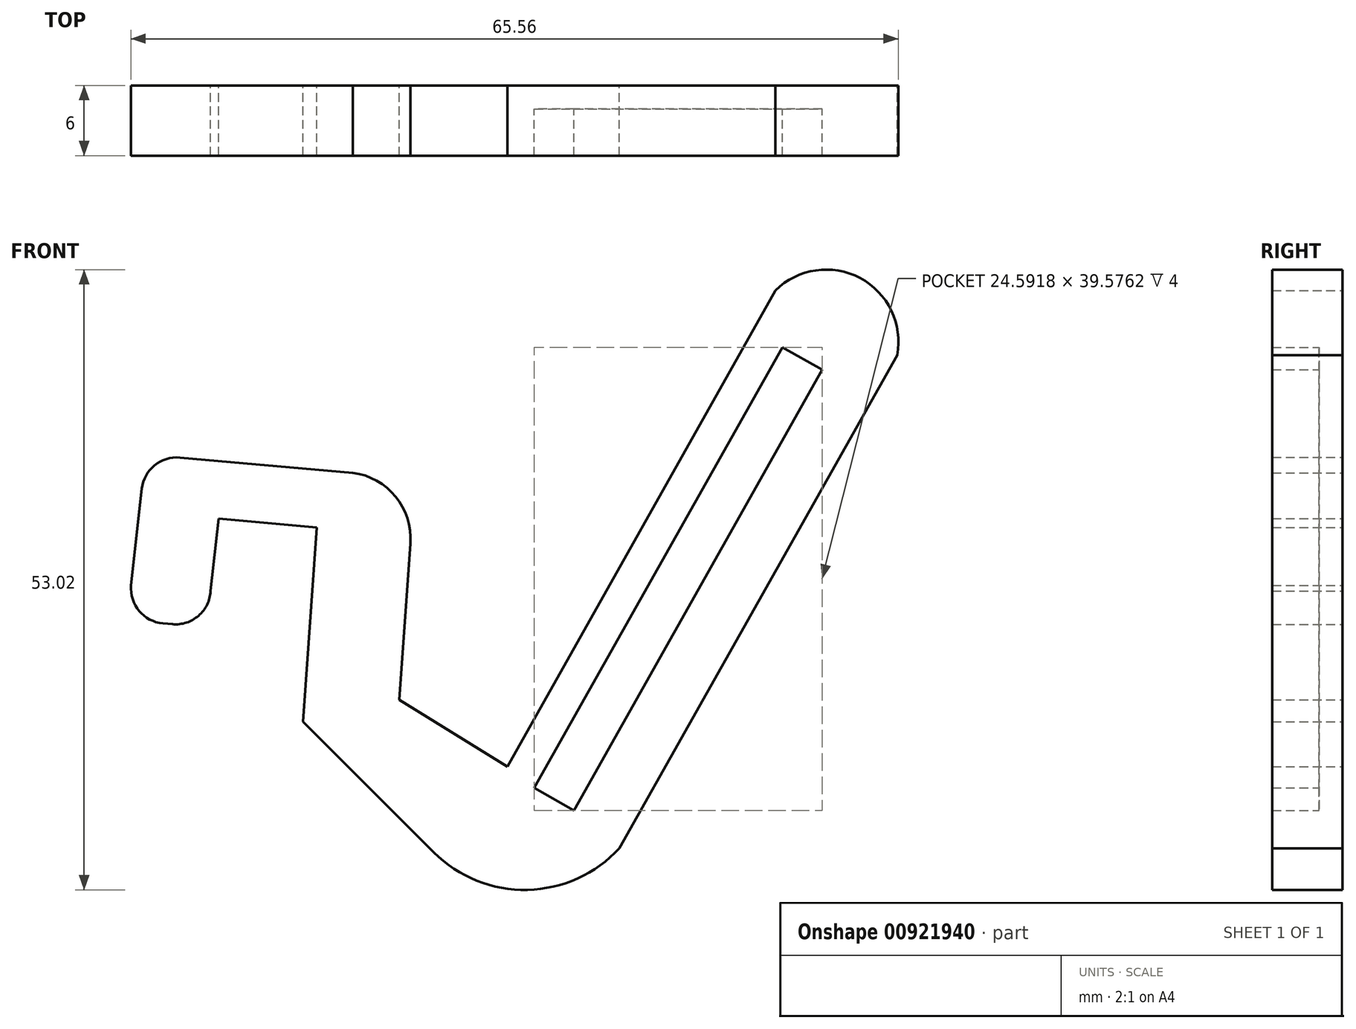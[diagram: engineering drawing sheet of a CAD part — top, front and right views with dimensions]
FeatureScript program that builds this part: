
annotation { "Feature Type Name" : "Feature", "Feature Type Description" : "" }
export const myFeature = defineFeature(function(context is Context, id is Id, definition is map)
    precondition{}
    {
        {
            var Q0;
            Q0=qCreatedBy(makeId("Front.planeOp"),FACE);
            var sketch = newSketch(context, id + "F0", { "sketchPlane" : qUnion([Q0])});
            skLineSegment(sketch, "E0", {"start": v(-33.3, 26.15) * mm, "end": v(-32.48, 26.08) * mm});
            skLineSegment(sketch, "E1", {"start": v(1.83, 10.17) * mm, "end": v(-1.57, 12.08) * mm});
            skLineSegment(sketch, "E2", {"start": v(-1.57, 12.08) * mm, "end": v(19.62, 49.74) * mm});
            skPoint(sketch, "E3.visualSharp", {"position": v(22.73, 46.46) * mm});
            skLineSegment(sketch, "E3.filletArc", {"start": v(24.58, 49.74) * mm, "end": v(24.58, 49.74) * mm});
            skPoint(sketch, "E4.visualSharp", {"position": v(27.2, 46.46) * mm});
            skLineSegment(sketch, "E4.filletArc", {"start": v(27.2, 46.46) * mm, "end": v(27.2, 46.46) * mm});
            skPoint(sketch, "E5.visualSharp", {"position": v(-21.33, 25.35) * mm});
            skArc(sketch, "E5.filletArc", {"start": v(-32.48, 26.08) * mm, "mid": v(-30.25, 26.8) * mm, "end": v(-29.23, 28.91) * mm});
            skPoint(sketch, "E6.visualSharp", {"position": v(-36.3, 26.15) * mm});
            skArc(sketch, "E6.filletArc", {"start": v(-36.02, 29.4) * mm, "mid": v(-35.33, 27.2) * mm, "end": v(-33.3, 26.15) * mm});
            skPoint(sketch, "E7.endSnap0", {"position": v(-22.65, 34.56) * mm});
            skPoint(sketch, "E8.visualSharp", {"position": v(-0.14, 38.58) * mm});
            skLineSegment(sketch, "E9", {"start": v(29.43, 49.09) * mm, "end": v(5.7, 6.93) * mm});
            skLineSegment(sketch, "E10", {"start": v(-1.47, 5.2) * mm, "end": v(-1.23, 4.71) * mm});
            skLineSegment(sketch, "E11.filletArc", {"start": v(32.4, 46.46) * mm, "end": v(32.4, 46.46) * mm});
            skLineSegment(sketch, "E12", {"start": v(19.62, 49.74) * mm, "end": v(23.02, 47.83) * mm});
            skPoint(sketch, "E13.endSnap0", {"position": v(29.8, 46.46) * mm});
            skArc(sketch, "E14.filletArc", {"start": v(32.47, 46.59) * mm, "mid": v(32.47, 46.6) * mm, "end": v(32.47, 46.6) * mm});
            skLineSegment(sketch, "E15", {"start": v(23.02, 47.83) * mm, "end": v(1.83, 10.17) * mm});
            skPoint(sketch, "E16.visualSharp", {"position": v(-13.23, 38.9) * mm});
            skLineSegment(sketch, "E16.filletArc", {"start": v(-12.65, 38.15) * mm, "end": v(-12.65, 38.15) * mm});
            skLineSegment(sketch, "E17", {"start": v(-28.54, 35.1) * mm, "end": v(-29.23, 28.91) * mm});
            skLineSegment(sketch, "E18", {"start": v(-36.02, 29.4) * mm, "end": v(-35.1, 37.67) * mm});
            skLineSegment(sketch, "E19", {"start": v(-31.85, 40.32) * mm, "end": v(-17.08, 39.02) * mm});
            skLineSegment(sketch, "E20", {"start": v(-20.15, 34.36) * mm, "end": v(-28.54, 35.1) * mm});
            skPoint(sketch, "E21.visualSharp", {"position": v(-34.77, 40.58) * mm});
            skArc(sketch, "E21.filletArc", {"start": v(-31.85, 40.32) * mm, "mid": v(-34.01, 39.66) * mm, "end": v(-35.1, 37.67) * mm});
            skLineSegment(sketch, "E22", {"start": v(-20.15, 34.36) * mm, "end": v(-21.33, 17.73) * mm});
            skLineSegment(sketch, "E23", {"start": v(-21.33, 17.73) * mm, "end": v(-10.16, 6.58) * mm});
            skArc(sketch, "E24", {"start": v(-10.16, 6.58) * mm, "mid": v(-2.16, 3.37) * mm, "end": v(5.7, 6.93) * mm});
            skLineSegment(sketch, "E25", {"start": v(-12.16, 33) * mm, "end": v(-13.11, 19.6) * mm});
            skLineSegment(sketch, "E26", {"start": v(-13.11, 19.6) * mm, "end": v(-3.88, 13.9) * mm});
            skLineSegment(sketch, "E27", {"start": v(-3.88, 13.9) * mm, "end": v(19.04, 54.61) * mm});
            skArc(sketch, "E28", {"start": v(29.43, 49.09) * mm, "mid": v(26.26, 55.67) * mm, "end": v(19.04, 54.61) * mm});
            skArc(sketch, "E29", {"start": v(-12.16, 33) * mm, "mid": v(-13.43, 36.99) * mm, "end": v(-17.08, 39.02) * mm});
            skSolve(sketch);
        }
        {
            var Q0;
            Q0=qSketchRegion(id+"F0",true);
            extrude(context, id + "F1", {"entities" : qUnion([Q0]), "depth" : 4 * mm, "offsetDistance" : 25 * mm});
        }
        {
            var Q0;
            Q0=makeQuery(id+"F0.imprint","IMPRINT",FACE,{"disambiguationData":[TD([[makeQuery(id+"F0.imprint","IMPRINT",EDGE,{"derivedFrom":sQuery(id+"F0.wireOp",EDGE,"E0")}),1.0]])]});
            var Q1;
            Q1=makeQuery(id+"F0.imprint","IMPRINT",FACE,{"disambiguationData":[TD([[makeQuery(id+"F0.imprint","IMPRINT",EDGE,{"derivedFrom":sQuery(id+"F0.wireOp",EDGE,"E1")}),-1.0]])]});
            extrude(context, id + "F2", {"entities" : qUnion([Q0, Q1]), "operationType" : NewBodyOperationType.ADD, "oppositeDirection" : true, "depth" : 2 * mm, "offsetDistance" : 25 * mm});
        }
    });
